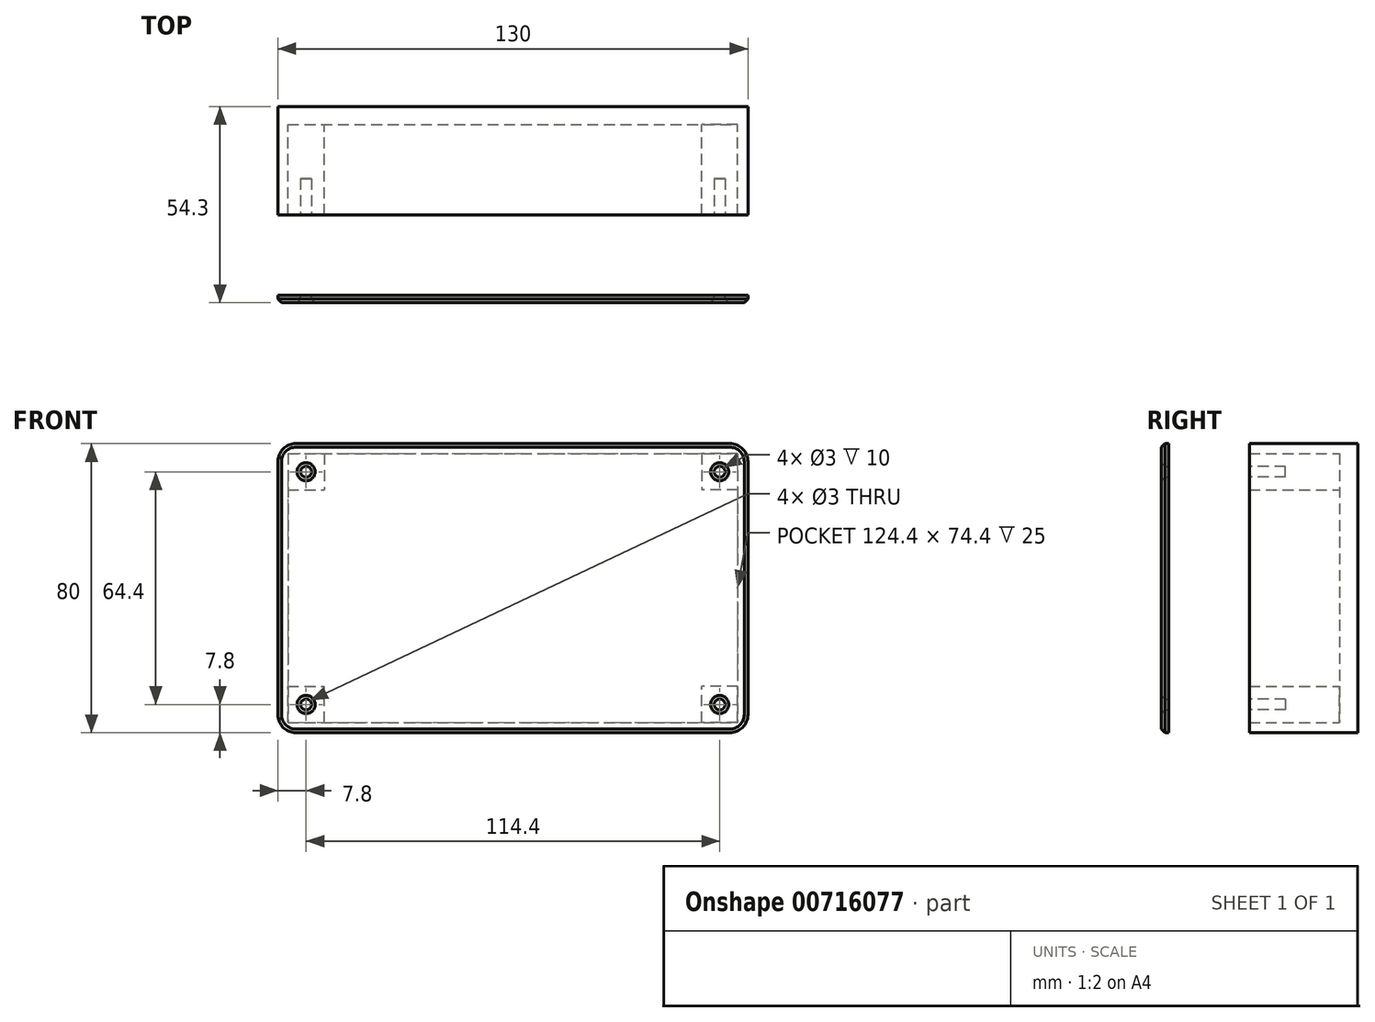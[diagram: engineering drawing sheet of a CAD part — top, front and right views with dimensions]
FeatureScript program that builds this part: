
annotation { "Feature Type Name" : "Feature", "Feature Type Description" : "" }
export const myFeature = defineFeature(function(context is Context, id is Id, definition is map)
    precondition{}
    {
        {
            var Q0;
            Q0=qCreatedBy(makeId("Front.planeOp"),FACE);
            var sketch = newSketch(context, id + "F0", { "sketchPlane" : qUnion([Q0])});
            skLineSegment(sketch, "E0.bottom", {"start": v(-60, 40) * mm, "end": v(60, 40) * mm});
            skLineSegment(sketch, "E0.top", {"start": v(-60, -40) * mm, "end": v(60, -40) * mm});
            skLineSegment(sketch, "E0.left", {"start": v(-65, 35) * mm, "end": v(-65, -35) * mm});
            skLineSegment(sketch, "E0.right", {"start": v(65, 35) * mm, "end": v(65, -35) * mm});
            skPoint(sketch, "E0.middle", {"position": v(0, 0) * mm});
            skPoint(sketch, "E1.visualSharp", {"position": v(65, -40) * mm});
            skArc(sketch, "E1.filletArc", {"start": v(60, -40) * mm, "mid": v(63.54, -38.54) * mm, "end": v(65, -35) * mm});
            skPoint(sketch, "E2.visualSharp", {"position": v(-65, -40) * mm});
            skArc(sketch, "E2.filletArc", {"start": v(-65, -35) * mm, "mid": v(-63.54, -38.54) * mm, "end": v(-60, -40) * mm});
            skPoint(sketch, "E3.visualSharp", {"position": v(65, 40) * mm});
            skArc(sketch, "E3.filletArc", {"start": v(65, 35) * mm, "mid": v(63.54, 38.54) * mm, "end": v(60, 40) * mm});
            skPoint(sketch, "E4.visualSharp", {"position": v(-65, 40) * mm});
            skArc(sketch, "E4.filletArc", {"start": v(-60, 40) * mm, "mid": v(-63.54, 38.54) * mm, "end": v(-65, 35) * mm});
            skSolve(sketch);
        }
        {
            var Q0;
            Q0=makeQuery(id+"F0.imprint","IMPRINT",FACE,{"disambiguationData":[TD([[makeQuery(id+"F0.imprint","IMPRINT",EDGE,{"derivedFrom":sQuery(id+"F0.wireOp",EDGE,"E0.bottom")}),-1.0]])]});
            extrude(context, id + "F1", {"entities" : qUnion([Q0]), "depth" : 5 * mm, "offsetDistance" : 25 * mm});
        }
        {
            var Q0;
            Q0=makeQuery(id+"F1.opExtrude","CAP_FACE",FACE,{"disambiguationData":[OSD([sQuery(id+"F0.wireOp",EDGE,"E0.bottom"),sQuery(id+"F0.wireOp",EDGE,"E0.top"),sQuery(id+"F0.wireOp",EDGE,"E0.left"),sQuery(id+"F0.wireOp",EDGE,"E0.right")])],"isStart":false});
            var sketch = newSketch(context, id + "F2", { "sketchPlane" : qUnion([Q0])});
            skLineSegment(sketch, "E5.0", {"start": v(-62.2, 37.2) * mm, "end": v(-62.2, -37.2) * mm});
            skLineSegment(sketch, "E5.1", {"start": v(-62.2, 37.2) * mm, "end": v(62.2, 37.2) * mm});
            skLineSegment(sketch, "E5.2", {"start": v(62.2, 37.2) * mm, "end": v(62.2, -37.2) * mm});
            skLineSegment(sketch, "E5.3", {"start": v(-62.2, -37.2) * mm, "end": v(62.2, -37.2) * mm});
            skSolve(sketch);
        }
        {
            var Q0;
            Q0=makeQuery(id+"F2.imprint","IMPRINT",FACE,{"disambiguationData":[TD([[makeQuery(id+"F2.imprint","IMPRINT",EDGE,{"derivedFrom":sQuery(id+"F2.wireOp",EDGE,"E5.0")}),-1.0]])]});
            extrude(context, id + "F3", {"entities" : qUnion([Q0]), "operationType" : NewBodyOperationType.ADD, "depth" : 25 * mm, "offsetDistance" : 25 * mm});
        }
        {
            var Q0;
            Q0=makeQuery(id+"F1.opExtrude","CAP_FACE",FACE,{"disambiguationData":[OSD([sQuery(id+"F0.wireOp",EDGE,"E0.bottom"),sQuery(id+"F0.wireOp",EDGE,"E0.top"),sQuery(id+"F0.wireOp",EDGE,"E0.left"),sQuery(id+"F0.wireOp",EDGE,"E0.right")])],"isStart":false});
            var sketch = newSketch(context, id + "F4", { "sketchPlane" : qUnion([Q0])});
            skLineSegment(sketch, "E6.bottom", {"start": v(-62.2, 37.2) * mm, "end": v(-52.2, 37.2) * mm});
            skLineSegment(sketch, "E6.top", {"start": v(-62.2, 27.2) * mm, "end": v(-52.2, 27.2) * mm});
            skLineSegment(sketch, "E6.left", {"start": v(-62.2, 37.2) * mm, "end": v(-62.2, 27.2) * mm});
            skLineSegment(sketch, "E6.right", {"start": v(-52.2, 37.2) * mm, "end": v(-52.2, 27.2) * mm});
            skSolve(sketch);
        }
        {
            var Q0;
            Q0=makeQuery(id+"F4.imprint","IMPRINT",FACE,{"disambiguationData":[TD([[makeQuery(id+"F4.imprint","IMPRINT",EDGE,{"derivedFrom":sQuery(id+"F4.wireOp",EDGE,"E6.bottom")}),-1.0]])]});
            extrude(context, id + "F5", {"entities" : qUnion([Q0]), "depth" : 25 * mm, "offsetDistance" : 25 * mm});
        }
        {
            var Q0;
            Q0=makeQuery(id+"F5.opExtrude","SWEPT_BODY",BODY,{"disambiguationData":[OSD([sQuery(id+"F4.wireOp",EDGE,"E6.bottom"),sQuery(id+"F4.wireOp",EDGE,"E6.top"),sQuery(id+"F4.wireOp",EDGE,"E6.left"),sQuery(id+"F4.wireOp",EDGE,"E6.right")])]});
            var Q1;
            Q1=qCreatedBy(makeId("Right.planeOp"),FACE);
            mirror(context, id + "F6", {"entities" : qUnion([Q0]), "mirrorPlane" : qUnion([Q1])});
        }
        {
            var Q0;
            Q0=makeQuery(id+"F5.opExtrude","SWEPT_BODY",BODY,{"disambiguationData":[OSD([sQuery(id+"F4.wireOp",EDGE,"E6.bottom"),sQuery(id+"F4.wireOp",EDGE,"E6.top"),sQuery(id+"F4.wireOp",EDGE,"E6.left"),sQuery(id+"F4.wireOp",EDGE,"E6.right")])]});
            var Q1;
            Q1=makeQuery(id+"F6.opPattern","COPY",BODY,{"derivedFrom":makeQuery(id+"F5.opExtrude","SWEPT_BODY",BODY,{"disambiguationData":[OSD([sQuery(id+"F4.wireOp",EDGE,"E6.bottom"),sQuery(id+"F4.wireOp",EDGE,"E6.top"),sQuery(id+"F4.wireOp",EDGE,"E6.left"),sQuery(id+"F4.wireOp",EDGE,"E6.right")])]}),"instanceName":"1"});
            var Q2;
            Q2=qCreatedBy(makeId("Top.planeOp"),FACE);
            mirror(context, id + "F7", {"entities" : qUnion([Q0, Q1]), "mirrorPlane" : qUnion([Q2])});
        }
        {
            var Q0;
            Q0=qCreatedBy(makeId("Front.planeOp"),FACE);
            cPlane(context, id + "F8", {"entities" : qUnion([Q0]), "cplaneType" : CPlaneType.OFFSET, "offset" : 52.3 * mm, "width" : 150 * mm, "height" : 150 * mm});
        }
        {
            var Q0;
            Q0=makeQuery(id+"F7.opPattern","COPY",BODY,{"derivedFrom":makeQuery(id+"F6.opPattern","COPY",BODY,{"derivedFrom":makeQuery(id+"F5.opExtrude","SWEPT_BODY",BODY,{"disambiguationData":[OSD([sQuery(id+"F4.wireOp",EDGE,"E6.bottom"),sQuery(id+"F4.wireOp",EDGE,"E6.top"),sQuery(id+"F4.wireOp",EDGE,"E6.left"),sQuery(id+"F4.wireOp",EDGE,"E6.right")])]}),"instanceName":"1"}),"instanceName":"1"});
            deleteBodies(context, id + "F9", {"entities" : qUnion([Q0])});
        }
        {
            var Q0;
            Q0=makeQuery(id+"F6.opPattern","COPY",BODY,{"derivedFrom":makeQuery(id+"F5.opExtrude","SWEPT_BODY",BODY,{"disambiguationData":[OSD([sQuery(id+"F4.wireOp",EDGE,"E6.bottom"),sQuery(id+"F4.wireOp",EDGE,"E6.top"),sQuery(id+"F4.wireOp",EDGE,"E6.left"),sQuery(id+"F4.wireOp",EDGE,"E6.right")])]}),"instanceName":"1"});
            deleteBodies(context, id + "F10", {"entities" : qUnion([Q0])});
        }
        {
            var Q0;
            Q0=makeQuery(id+"F7.opPattern","COPY",BODY,{"derivedFrom":makeQuery(id+"F5.opExtrude","SWEPT_BODY",BODY,{"disambiguationData":[OSD([sQuery(id+"F4.wireOp",EDGE,"E6.bottom"),sQuery(id+"F4.wireOp",EDGE,"E6.top"),sQuery(id+"F4.wireOp",EDGE,"E6.left"),sQuery(id+"F4.wireOp",EDGE,"E6.right")])]}),"instanceName":"1"});
            deleteBodies(context, id + "F11", {"entities" : qUnion([Q0])});
        }
        {
            var Q0;
            Q0=makeQuery(id+"F5.opExtrude","CAP_FACE",FACE,{"disambiguationData":[OSD([sQuery(id+"F4.wireOp",EDGE,"E6.bottom"),sQuery(id+"F4.wireOp",EDGE,"E6.top"),sQuery(id+"F4.wireOp",EDGE,"E6.left"),sQuery(id+"F4.wireOp",EDGE,"E6.right")])],"isStart":false});
            var sketch = newSketch(context, id + "F12", { "sketchPlane" : qUnion([Q0])});
            skCircle(sketch, "E7", {"center": v(-57.2, 32.2) * mm, "radius": 1.5 * mm});
            skPoint(sketch, "E7.centerSnap0", {"position": v(-52.2, 32.2) * mm});
            skPoint(sketch, "E7.centerSnap1", {"position": v(-57.2, 27.2) * mm});
            skSolve(sketch);
        }
        {
            var Q0;
            Q0=makeQuery(id+"F12.imprint","IMPRINT",FACE,{"disambiguationData":[TD([[makeQuery(id+"F12.imprint","IMPRINT",EDGE,{"derivedFrom":sQuery(id+"F12.wireOp",EDGE,"E7")}),1.0]])]});
            extrude(context, id + "F13", {"entities" : qUnion([Q0]), "operationType" : NewBodyOperationType.REMOVE, "oppositeDirection" : true, "depth" : 10 * mm, "offsetDistance" : 25 * mm});
        }
        {
            var Q0;
            Q0=makeQuery(id+"F5.opExtrude","SWEPT_BODY",BODY,{"disambiguationData":[OSD([sQuery(id+"F4.wireOp",EDGE,"E6.bottom"),sQuery(id+"F4.wireOp",EDGE,"E6.top"),sQuery(id+"F4.wireOp",EDGE,"E6.left"),sQuery(id+"F4.wireOp",EDGE,"E6.right")])]});
            var Q1;
            Q1=qCreatedBy(makeId("Top.planeOp"),FACE);
            mirror(context, id + "F14", {"entities" : qUnion([Q0]), "mirrorPlane" : qUnion([Q1])});
        }
        {
            var Q0;
            Q0=makeQuery(id+"F14.opPattern","COPY",BODY,{"derivedFrom":makeQuery(id+"F5.opExtrude","SWEPT_BODY",BODY,{"disambiguationData":[OSD([sQuery(id+"F4.wireOp",EDGE,"E6.bottom"),sQuery(id+"F4.wireOp",EDGE,"E6.top"),sQuery(id+"F4.wireOp",EDGE,"E6.left"),sQuery(id+"F4.wireOp",EDGE,"E6.right")])]}),"instanceName":"1"});
            var Q1;
            Q1=makeQuery(id+"F5.opExtrude","SWEPT_BODY",BODY,{"disambiguationData":[OSD([sQuery(id+"F4.wireOp",EDGE,"E6.bottom"),sQuery(id+"F4.wireOp",EDGE,"E6.top"),sQuery(id+"F4.wireOp",EDGE,"E6.left"),sQuery(id+"F4.wireOp",EDGE,"E6.right")])]});
            var Q2;
            Q2=qCreatedBy(makeId("Right.planeOp"),FACE);
            mirror(context, id + "F15", {"entities" : qUnion([Q0, Q1]), "mirrorPlane" : qUnion([Q2])});
        }
        {
            var Q0;
            Q0=qCreatedBy(id+"F8.planeOp",FACE);
            var sketch = newSketch(context, id + "F16", { "sketchPlane" : qUnion([Q0])});
            skCircle(sketch, "E8.0.0", {"center": v(-57.2, -32.2) * mm, "radius": 1.5 * mm});
            skCircle(sketch, "E8.1.0", {"center": v(57.2, -32.2) * mm, "radius": 1.5 * mm});
            skCircle(sketch, "E8.2.0", {"center": v(57.2, 32.2) * mm, "radius": 1.5 * mm});
            skCircle(sketch, "E8.3.0", {"center": v(-57.2, 32.2) * mm, "radius": 1.5 * mm});
            skLineSegment(sketch, "E9.0.0", {"start": v(-65, 35) * mm, "end": v(-65, -35) * mm});
            skArc(sketch, "E9.0.1", {"start": v(-65, -35) * mm, "mid": v(-63.54, -38.54) * mm, "end": v(-60, -40) * mm});
            skLineSegment(sketch, "E9.0.2", {"start": v(-60, -40) * mm, "end": v(60, -40) * mm});
            skArc(sketch, "E9.0.3", {"start": v(60, -40) * mm, "mid": v(63.54, -38.54) * mm, "end": v(65, -35) * mm});
            skLineSegment(sketch, "E9.0.4", {"start": v(65, -35) * mm, "end": v(65, 35) * mm});
            skArc(sketch, "E9.0.5", {"start": v(65, 35) * mm, "mid": v(63.54, 38.54) * mm, "end": v(60, 40) * mm});
            skLineSegment(sketch, "E9.0.6", {"start": v(60, 40) * mm, "end": v(-60, 40) * mm});
            skArc(sketch, "E9.0.7", {"start": v(-60, 40) * mm, "mid": v(-63.54, 38.54) * mm, "end": v(-65, 35) * mm});
            skSolve(sketch);
        }
        {
            var Q0;
            Q0=makeQuery(id+"F16.imprint","IMPRINT",FACE,{"disambiguationData":[TD([[makeQuery(id+"F16.imprint","IMPRINT",EDGE,{"derivedFrom":sQuery(id+"F16.wireOp",EDGE,"E8.0.0")}),-1.0]])]});
            extrude(context, id + "F17", {"entities" : qUnion([Q0]), "depth" : 2 * mm, "offsetDistance" : 25 * mm});
        }
        {
            var Q0;
            Q0=makeQuery(id+"F17.opExtrude","CAP_FACE",FACE,{"disambiguationData":[OSD([sQuery(id+"F16.wireOp",EDGE,"E8.0.0"),sQuery(id+"F16.wireOp",EDGE,"E8.1.0"),sQuery(id+"F16.wireOp",EDGE,"E8.2.0"),sQuery(id+"F16.wireOp",EDGE,"E8.3.0"),sQuery(id+"F16.wireOp",EDGE,"E9.0.0"),sQuery(id+"F16.wireOp",EDGE,"E9.0.1"),sQuery(id+"F16.wireOp",EDGE,"E9.0.2"),sQuery(id+"F16.wireOp",EDGE,"E9.0.3"),sQuery(id+"F16.wireOp",EDGE,"E9.0.4"),sQuery(id+"F16.wireOp",EDGE,"E9.0.5"),sQuery(id+"F16.wireOp",EDGE,"E9.0.6"),sQuery(id+"F16.wireOp",EDGE,"E9.0.7")])],"isStart":false});
            chamfer(context, id + "F18", {"entities" : qUnion([Q0]), "width" : 1 * mm, "tangentPropagation" : true});
        }
    });
